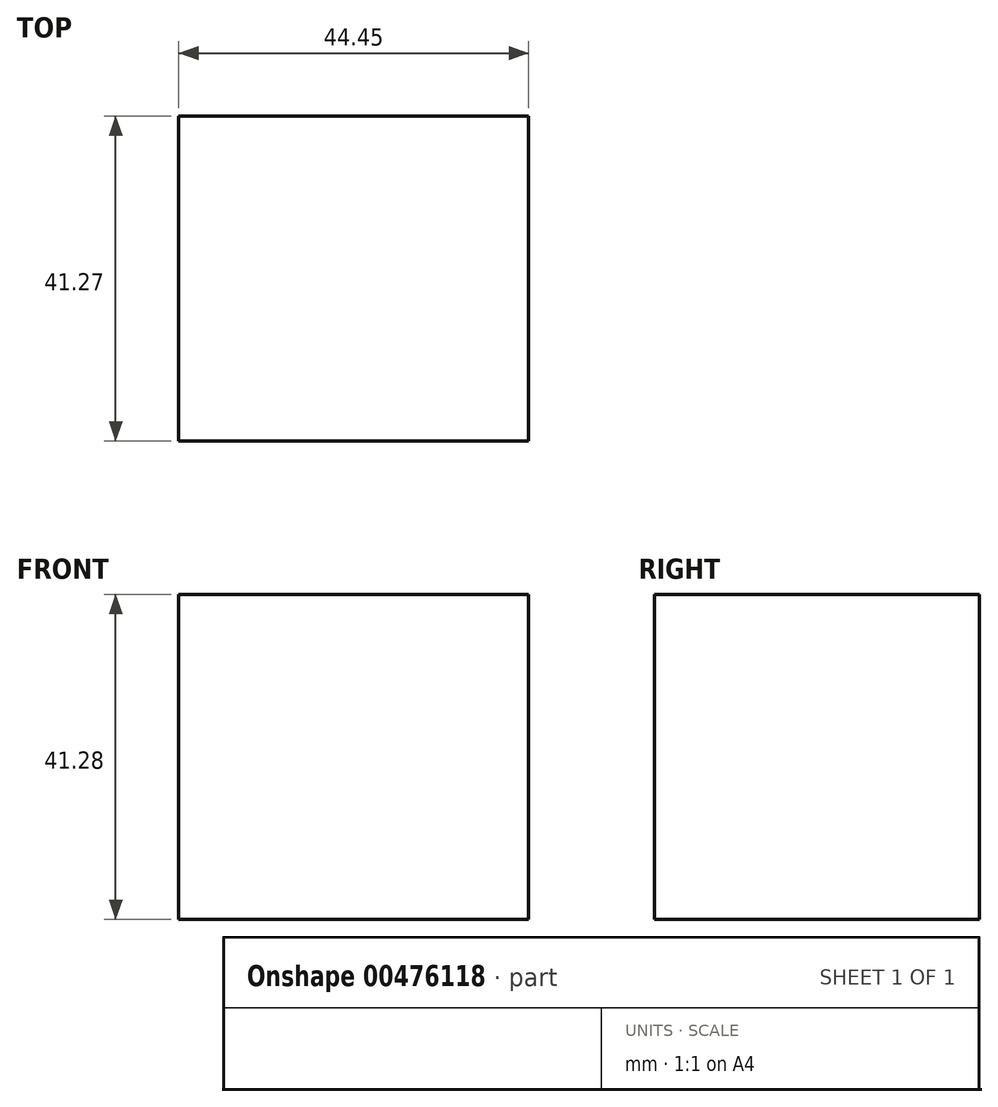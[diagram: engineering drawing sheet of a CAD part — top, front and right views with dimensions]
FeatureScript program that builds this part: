
annotation { "Feature Type Name" : "Feature", "Feature Type Description" : "" }
export const myFeature = defineFeature(function(context is Context, id is Id, definition is map)
    precondition{}
    {
        {
            var Q0;
            Q0=qCreatedBy(makeId("Front.planeOp"),FACE);
            var sketch = newSketch(context, id + "F0", { "sketchPlane" : qUnion([Q0])});
            skLineSegment(sketch, "E0.bottom", {"start": v(-20.64, 20.64) * mm, "end": v(20.64, 20.64) * mm});
            skLineSegment(sketch, "E0.top", {"start": v(-20.64, -20.64) * mm, "end": v(20.64, -20.64) * mm});
            skLineSegment(sketch, "E0.left", {"start": v(-20.64, 20.64) * mm, "end": v(-20.64, -20.64) * mm});
            skLineSegment(sketch, "E0.right", {"start": v(20.64, 20.64) * mm, "end": v(20.64, -20.64) * mm});
            skPoint(sketch, "E0.middle", {"position": v(0, 0) * mm});
            skSolve(sketch);
        }
        {
            var Q0;
            Q0=makeQuery(id+"F0.imprint","IMPRINT",FACE,{"disambiguationData":[TD([[makeQuery(id+"F0.imprint","IMPRINT",EDGE,{"derivedFrom":sQuery(id+"F0.wireOp",EDGE,"E0.bottom")}),-1.0]])]});
            extrude(context, id + "F1", {"entities" : qUnion([Q0]), "depth" : 41.27 * mm});
        }
        {
            var Q0;
            Q0=makeQuery(id+"F1.opExtrude","SWEPT_FACE",FACE,{"disambiguationData":[OSD([sQuery(id+"F0.wireOp",EDGE,"E0.right")])]});
            extrude(context, id + "F2", {"entities" : qUnion([Q0]), "operationType" : NewBodyOperationType.REMOVE, "oppositeDirection" : true, "depth" : 38.1 * mm});
        }
        {
            var Q0;
            Q0=makeQuery(id+"F2.boolean.opBoolean","COPY",FACE,{"derivedFrom":makeQuery(id+"F2.opExtrude","CAP_FACE",FACE,{"disambiguationData":[OSD([sQuery(id+"F0.wireOp",EDGE,"E0.right")])],"isStart":false})});
            extrude(context, id + "F3", {"entities" : qUnion([Q0]), "operationType" : NewBodyOperationType.ADD, "depth" : 41.27 * mm});
        }
        {
            var Q0;
            Q0=makeQuery(id+"F3.opExtrude","CAP_FACE",FACE,{"disambiguationData":[OSD([sQuery(id+"F0.wireOp",EDGE,"E0.right")])],"isStart":false});
            extrude(context, id + "F4", {"entities" : qUnion([Q0]), "operationType" : NewBodyOperationType.ADD, "oppositeDirection" : true, "depth" : 15.88 * mm});
        }
    });
